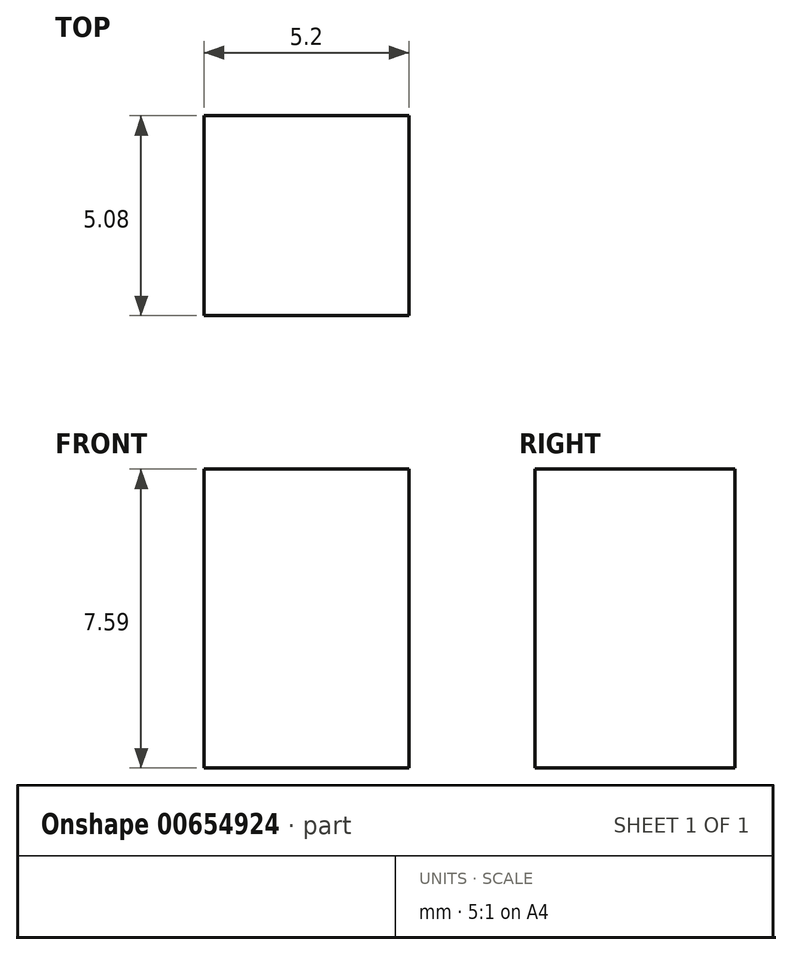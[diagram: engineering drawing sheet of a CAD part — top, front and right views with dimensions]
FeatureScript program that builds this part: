
annotation { "Feature Type Name" : "Feature", "Feature Type Description" : "" }
export const myFeature = defineFeature(function(context is Context, id is Id, definition is map)
    precondition{}
    {
        {
            var Q0;
            Q0=qCreatedBy(makeId("Front.planeOp"),FACE);
            var sketch = newSketch(context, id + "F0", { "sketchPlane" : qUnion([Q0])});
            skLineSegment(sketch, "E0", {"start": v(0, 0) * mm, "end": v(5.2, 0) * mm});
            skLineSegment(sketch, "E1", {"start": v(5.2, 0) * mm, "end": v(5.2, 7.6) * mm});
            skLineSegment(sketch, "E2", {"start": v(5.2, 7.6) * mm, "end": v(0, 7.6) * mm});
            skLineSegment(sketch, "E3", {"start": v(0, 7.6) * mm, "end": v(0, 0) * mm});
            skSolve(sketch);
        }
        {
            var Q0;
            Q0=makeQuery(id+"F0.imprint","IMPRINT",FACE,{"disambiguationData":[TD([[makeQuery(id+"F0.imprint","IMPRINT",EDGE,{"derivedFrom":sQuery(id+"F0.wireOp",EDGE,"E0")}),1.0]])]});
            extrude(context, id + "F1", {"entities" : qUnion([Q0]), "depth" : 5.08 * mm, "offsetDistance" : 25.4 * mm});
        }
    });
